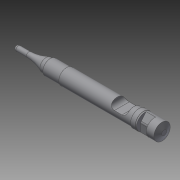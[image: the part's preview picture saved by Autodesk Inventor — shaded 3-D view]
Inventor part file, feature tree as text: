
AUTODESK INVENTOR PART (.ipt)
format: ipt  version: 2014 SP1 (Build 180222100, 222)  size: 158,720 bytes
history: native  units: in
note: dims shown in document units (in); Inventor stores cm internally (conversion verified against a paired STEP export)
features: sketch x3, extrude x2, projected_geometry x2, revolve x1, plane x1, fillet x1
ambient origin geometry x8: Origin, YZ Plane, XZ Plane, XY Plane, X Axis, Y Axis, Z Axis, Center Point
bodies: Solid1 (feature_tree)
feature tree (10):
  revolve  "Revolution1"  [1 undecoded]
  extrude  "Extrusion1"  Depth=0.2055in
  plane  "Work Plane1"
  extrude  "Extrusion2"  Depth=0.0362in
  fillet  "Fillet1"  Radius=0.07in
  sketch  "Sketch1"  dims[d0=2.0695in d1=0.069in]
  sketch  "Sketch2"  dims[d2=0.1745in d3=0.2055in]
  sketch  "Sketch3"  dims[d4=0.216in d5=0.234in d6=0.07in d7=0.7559in d8=0.2875in d9=0.0648in d10=0.2285in d11=1.075in d12=0.479in d13=0.422in d14=0.18in d15=90.0deg d16=0.0625in d17=0.2315in d18=0.1345in d19=0.938in d20=1.0in d21=0.0in d22=0.019in d23=0.962in d24=0.1735in d25=0.133in d26=0.0in d27=0.0362in]
  projected_geometry  "Project Cut Edges1"
  projected_geometry  "Project Cut Edges2"
note: 1 required parameter value undecoded (feature->parameter linkage not recoverable at this tier; creation-order binding heuristic only, values carry confidence <= 0.55)
